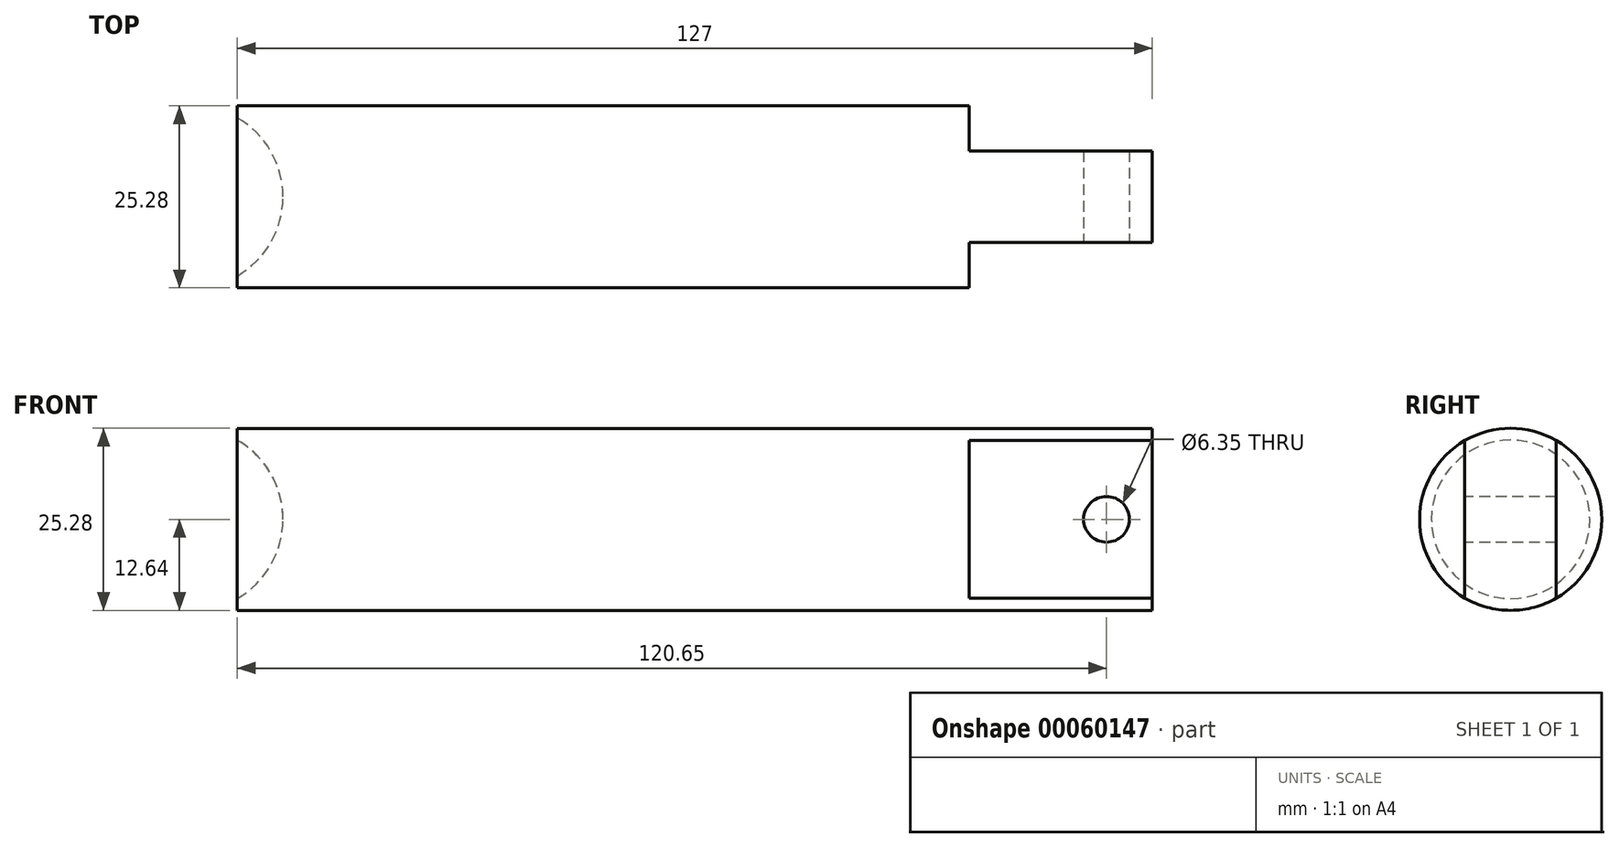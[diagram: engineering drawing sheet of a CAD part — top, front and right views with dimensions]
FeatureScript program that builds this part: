
annotation { "Feature Type Name" : "Feature", "Feature Type Description" : "" }
export const myFeature = defineFeature(function(context is Context, id is Id, definition is map)
    precondition{}
    {
        {
            var Q0;
            Q0=qCreatedBy(makeId("Front.planeOp"),FACE);
            var sketch = newSketch(context, id + "F0", { "sketchPlane" : qUnion([Q0])});
            skLineSegment(sketch, "E0.bottom", {"start": v(0, 0) * mm, "end": v(-127, 0) * mm});
            skLineSegment(sketch, "E0.top", {"start": v(0, 12.64) * mm, "end": v(-127, 12.64) * mm});
            skLineSegment(sketch, "E0.left", {"start": v(0, 0) * mm, "end": v(0, 12.64) * mm});
            skLineSegment(sketch, "E0.right", {"start": v(-127, 0) * mm, "end": v(-127, 12.64) * mm});
            skSolve(sketch);
        }
        {
            var Q0;
            Q0 = qSketchRegion(id + "F0", true);
            var Q1;
            Q1=sQuery(id+"F0.wireOp",EDGE,"E0.bottom");
            revolve(context, id + "F1", {"entities" : qUnion([Q0]), "axis" : qUnion([Q1]), "revolveType" : RevolveType.FULL});
        }
        {
            var Q0;
            Q0=makeQuery(id+"F1.opRevolve","SWEPT_FACE",FACE,{"disambiguationData":[OSD([sQuery(id+"F0.wireOp",EDGE,"E0.left")])]});
            var sketch = newSketch(context, id + "F2", { "sketchPlane" : qUnion([Q0])});
            skLineSegment(sketch, "E1.bottom", {"start": v(-39.77, 25.9) * mm, "end": v(-6.35, 25.9) * mm});
            skLineSegment(sketch, "E1.top", {"start": v(-39.77, -27.9) * mm, "end": v(-6.35, -27.9) * mm});
            skLineSegment(sketch, "E1.left", {"start": v(-39.77, 25.9) * mm, "end": v(-39.77, -27.9) * mm});
            skLineSegment(sketch, "E1.right", {"start": v(-6.35, 25.9) * mm, "end": v(-6.35, -27.9) * mm});
            skLineSegment(sketch, "E2.bottom", {"start": v(6.35, -31.92) * mm, "end": v(52.14, -31.92) * mm});
            skLineSegment(sketch, "E2.top", {"start": v(6.35, 43.61) * mm, "end": v(52.14, 43.61) * mm});
            skLineSegment(sketch, "E2.left", {"start": v(6.35, -31.92) * mm, "end": v(6.35, 43.61) * mm});
            skLineSegment(sketch, "E2.right", {"start": v(52.14, -31.92) * mm, "end": v(52.14, 43.61) * mm});
            skSolve(sketch);
        }
        {
            var Q0;
            Q0 = qSketchRegion(id + "F2", true);
            extrude(context, id + "F3", {"entities" : qUnion([Q0]), "operationType" : NewBodyOperationType.REMOVE, "oppositeDirection" : true, "depth" : 25.4 * mm});
        }
        {
            var Q0;
            Q0=makeQuery(id+"F3.boolean.opBoolean","COPY",FACE,{"derivedFrom":makeQuery(id+"F3.opExtrude","SWEPT_FACE",FACE,{"disambiguationData":[OSD([sQuery(id+"F2.wireOp",EDGE,"E1.right")])]})});
            var sketch = newSketch(context, id + "F4", { "sketchPlane" : qUnion([Q0])});
            skCircle(sketch, "E3", {"center": v(-6.35, 0) * mm, "radius": 3.18 * mm});
            skSolve(sketch);
        }
        {
            var Q0;
            Q0 = qSketchRegion(id + "F4", true);
            extrude(context, id + "F5", {"entities" : qUnion([Q0]), "operationType" : NewBodyOperationType.REMOVE, "oppositeDirection" : true, "depth" : 25.4 * mm});
        }
        {
            var Q0;
            Q0=qCreatedBy(makeId("Front.planeOp"),FACE);
            var sketch = newSketch(context, id + "F6", { "sketchPlane" : qUnion([Q0])});
            skArc(sketch, "E4", {"start": v(-146.05, 0) * mm, "mid": v(-133.35, -12.7) * mm, "end": v(-120.65, 0) * mm});
            skLineSegment(sketch, "E5", {"start": v(-120.65, 0) * mm, "end": v(-146.05, 0) * mm});
            skSolve(sketch);
        }
        {
            var Q0;
            Q0 = qSketchRegion(id + "F6", true);
            var Q1;
            Q1=sQuery(id+"F6.wireOp",EDGE,"E5");
            revolve(context, id + "F7", {"operationType" : NewBodyOperationType.REMOVE, "entities" : qUnion([Q0]), "axis" : qUnion([Q1]), "revolveType" : RevolveType.FULL, "oppositeDirection" : true});
        }
    });
